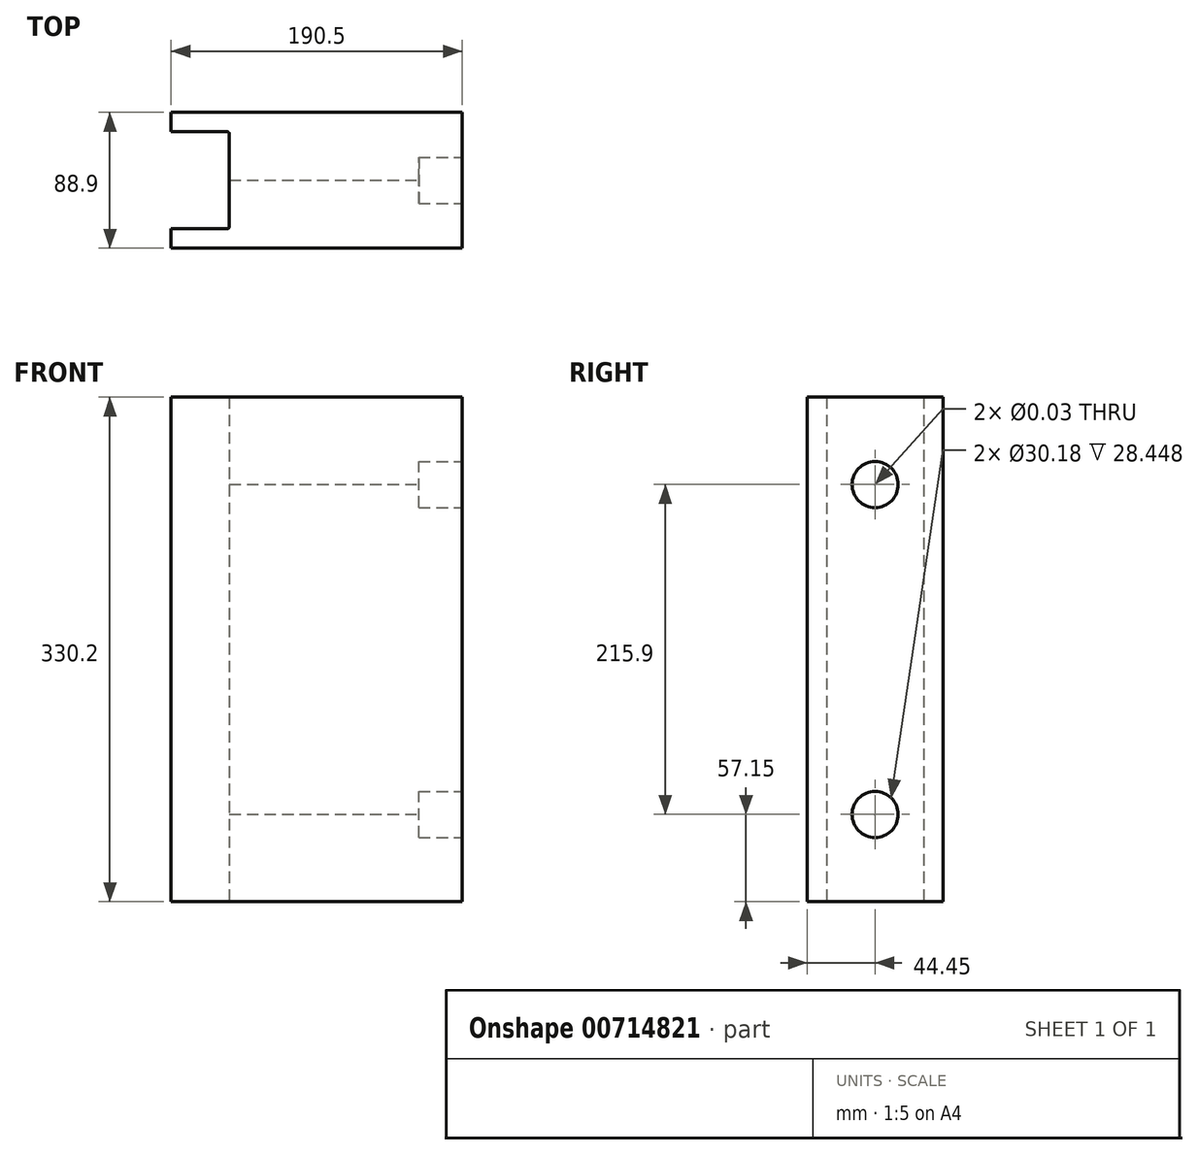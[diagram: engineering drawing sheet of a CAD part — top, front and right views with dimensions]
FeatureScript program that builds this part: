
annotation { "Feature Type Name" : "Feature", "Feature Type Description" : "" }
export const myFeature = defineFeature(function(context is Context, id is Id, definition is map)
    precondition{}
    {
        {
            var Q0;
            Q0=qCreatedBy(makeId("Top.planeOp"),FACE);
            var sketch = newSketch(context, id + "F0", { "sketchPlane" : qUnion([Q0])});
            skLineSegment(sketch, "E0.bottom", {"start": v(-95.25, 44.45) * mm, "end": v(95.25, 44.45) * mm});
            skLineSegment(sketch, "E0.top", {"start": v(-95.25, -44.45) * mm, "end": v(95.25, -44.45) * mm});
            skLineSegment(sketch, "E0.left", {"start": v(-95.25, 44.45) * mm, "end": v(-95.25, 31.75) * mm});
            skLineSegment(sketch, "E0.right", {"start": v(95.25, 44.45) * mm, "end": v(95.25, -44.45) * mm});
            skPoint(sketch, "E0.middle", {"position": v(0, 0) * mm});
            skLineSegment(sketch, "E1.bottom", {"start": v(-133.35, 31.75) * mm, "end": v(-57.15, 31.75) * mm});
            skLineSegment(sketch, "E1.top", {"start": v(-133.35, -31.75) * mm, "end": v(-57.15, -31.75) * mm});
            skLineSegment(sketch, "E1.right", {"start": v(-57.15, 31.75) * mm, "end": v(-57.15, -31.75) * mm});
            skPoint(sketch, "E1.middle", {"position": v(-95.25, 0) * mm});
            skLineSegment(sketch, "E2.trimOffspring", {"start": v(-95.25, -31.75) * mm, "end": v(-95.25, -44.45) * mm});
            skSolve(sketch);
        }
        {
            var Q0;
            Q0=qSketchRegion(id+"F0",true);
            extrude(context, id + "F1", {"entities" : qUnion([Q0]), "endBound" : BoundingType.SYMMETRIC, "depth" : 330.2 * mm, "offsetDistance" : 25.4 * mm});
        }
        {
            var Q0;
            Q0=makeQuery(id+"F1.opExtrude","SWEPT_FACE",FACE,{"disambiguationData":[OSD([sQuery(id+"F0.wireOp",EDGE,"E0.right")])]});
            var sketch = newSketch(context, id + "F2", { "sketchPlane" : qUnion([Q0])});
            skLineSegment(sketch, "E3.0", {"start": v(44.45, 165.1) * mm, "end": v(-44.45, 165.1) * mm, "construction": true});
            skLineSegment(sketch, "E4", {"start": v(0, 167.27) * mm, "end": v(0, -162.09) * mm, "construction": true});
            skPoint(sketch, "E5.0", {"position": v(-31.75, -165.1) * mm});
            skLineSegment(sketch, "E6.0", {"start": v(44.45, -165.1) * mm, "end": v(-44.45, -165.1) * mm, "construction": true});
            skLineSegment(sketch, "E7.0", {"start": v(44.45, 107.95) * mm, "end": v(-44.45, 107.95) * mm, "construction": true});
            skLineSegment(sketch, "E8.0", {"start": v(44.45, -107.95) * mm, "end": v(-44.45, -107.95) * mm, "construction": true});
            skPoint(sketch, "E9", {"position": v(0, 107.95) * mm});
            skPoint(sketch, "E10", {"position": v(0, -107.95) * mm});
            skSolve(sketch);
        }
        {
            var Q0;
            Q0=sQuery(id+"F2.wireOp",VERTEX,"E9");
            var Q1;
            Q1=sQuery(id+"F2.wireOp",VERTEX,"E10");
            var Q2;
            Q2=makeQuery(id+"F1.opExtrude","SWEPT_BODY",BODY,{"disambiguationData":[OSD([sQuery(id+"F0.wireOp",EDGE,"E0.bottom"),sQuery(id+"F0.wireOp",EDGE,"E0.top"),sQuery(id+"F0.wireOp",EDGE,"E0.left"),sQuery(id+"F0.wireOp",EDGE,"E0.right"),sQuery(id+"F0.wireOp",EDGE,"E1.bottom"),sQuery(id+"F0.wireOp",EDGE,"E1.top"),sQuery(id+"F0.wireOp",EDGE,"E1.right"),sQuery(id+"F0.wireOp",EDGE,"E2.trimOffspring")])]});
            hole(context, id + "F3", {"style" : HoleStyle.C_BORE, "endStyle" : HoleEndStyle.THROUGH, "standardTappedOrClearance" : lookupTablePath({ "standard" : "ANSI", "size" : "13/16 (0.81)", "type" : "Drilled" }), "standardBlindInLast" : lookupTablePath({ "standard" : "ANSI", "size" : "13/16", "type" : "Drilled" }), "holeDiameter" : 13 / 406.4 * mm, "cBoreDiameter" : 30.18 * mm, "cBoreDepth" : 28.45 * mm, "majorDiameter" : 6.35 * mm, "isTappedThrough" : true, "tappedDepth" : 34.3 * mm, "tapClearance" : 3, "locations" : qUnion([Q0, Q1]), "scope" : qUnion([Q2])});
        }
        {
            var Q0;
            Q0=makeQuery(id+"F1.opExtrude","SWEPT_EDGE",EDGE,{"disambiguationData":[OSD([sQuery(id+"F0.wireOp",EDGE,"E1.bottom"),sQuery(id+"F0.wireOp",EDGE,"E1.right")])]});
            var Q1;
            Q1=makeQuery(id+"F1.opExtrude","SWEPT_EDGE",EDGE,{"disambiguationData":[OSD([sQuery(id+"F0.wireOp",EDGE,"E1.top"),sQuery(id+"F0.wireOp",EDGE,"E1.right")])]});
            fillet(context, id + "F4", {"entities" : qUnion([Q0, Q1]), "radius" : 1.52 * mm, "tangentPropagation" : true, "allowEdgeOverflow" : false});
        }
    });
